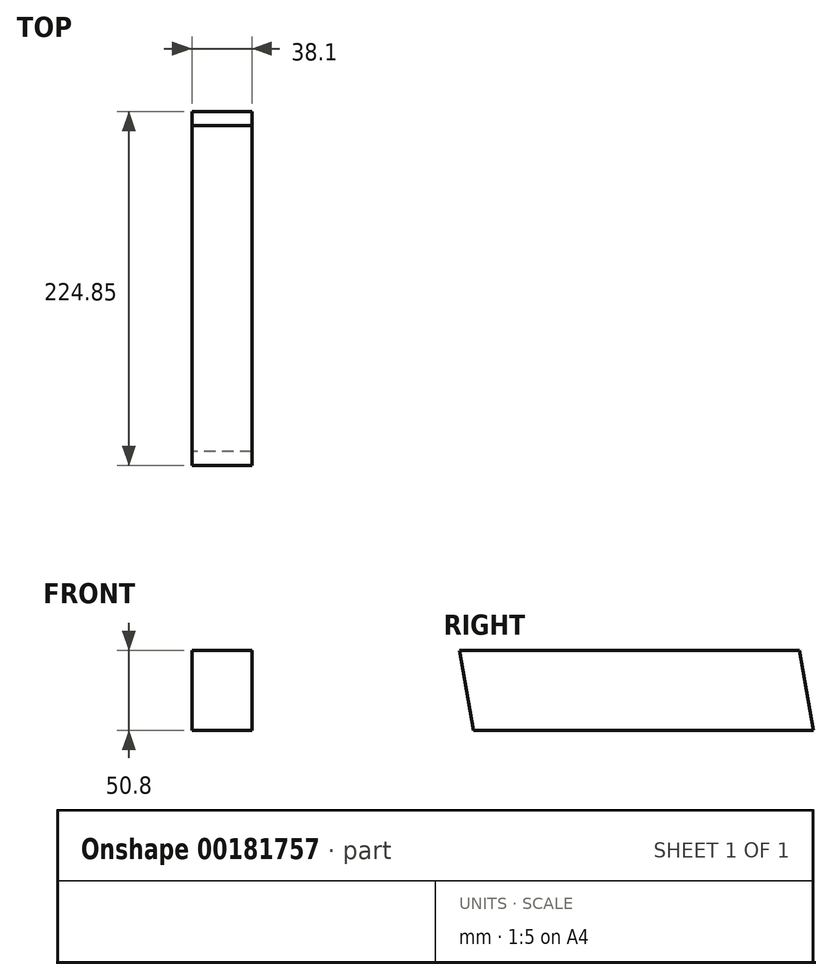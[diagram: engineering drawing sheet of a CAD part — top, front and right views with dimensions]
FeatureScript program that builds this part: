
annotation { "Feature Type Name" : "Feature", "Feature Type Description" : "" }
export const myFeature = defineFeature(function(context is Context, id is Id, definition is map)
    precondition{}
    {
        {
            var Q0;
            Q0=qCreatedBy(makeId("Right.planeOp"),FACE);
            var sketch = newSketch(context, id + "F0", { "sketchPlane" : qUnion([Q0])});
            skLineSegment(sketch, "E0.bottom", {"start": v(-117.5, 0) * mm, "end": v(98.4, 0) * mm});
            skLineSegment(sketch, "E0.top", {"start": v(-126.46, 50.8) * mm, "end": v(89.44, 50.8) * mm});
            skLineSegment(sketch, "E1", {"start": v(-126.46, 50.8) * mm, "end": v(-117.5, 0) * mm});
            skPoint(sketch, "E2.orphan", {"position": v(-126.46, 0) * mm});
            skLineSegment(sketch, "E3", {"start": v(98.4, 0) * mm, "end": v(89.44, 50.8) * mm});
            skSolve(sketch);
        }
        {
            var Q0;
            Q0 = qSketchRegion(id + "F0", true);
            extrude(context, id + "F1", {"entities" : qUnion([Q0]), "depth" : 38.1 * mm});
        }
    });
